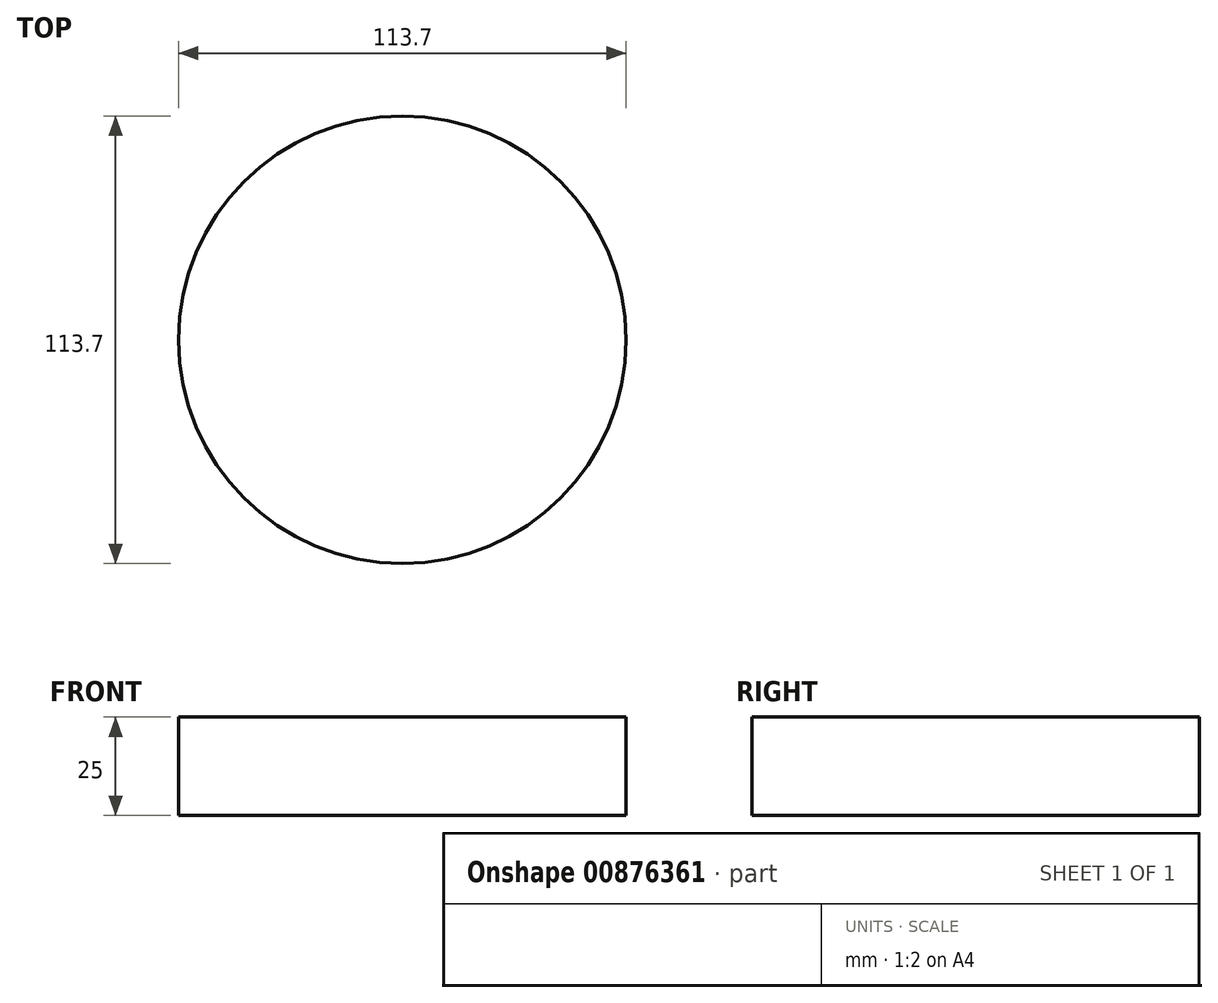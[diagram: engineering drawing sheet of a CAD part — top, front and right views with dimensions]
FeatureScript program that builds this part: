
annotation { "Feature Type Name" : "Feature", "Feature Type Description" : "" }
export const myFeature = defineFeature(function(context is Context, id is Id, definition is map)
    precondition{}
    {
        {
            var Q0;
            Q0=qCreatedBy(makeId("Top.planeOp"),FACE);
            var sketch = newSketch(context, id + "F0", { "sketchPlane" : qUnion([Q0])});
            skCircle(sketch, "E0", {"center": v(0, 0) * mm, "radius": 56.85 * mm});
            skLineSegment(sketch, "E1", {"start": v(0, 0) * mm, "end": v(-47.95, -30.54) * mm});
            skLineSegment(sketch, "E2", {"start": v(0, 0) * mm, "end": v(46.28, 29.47) * mm});
            skLineSegment(sketch, "E3", {"start": v(34.44, -45.23) * mm, "end": v(-46.7, -32.42) * mm});
            skLineSegment(sketch, "E4", {"start": v(-46.7, -32.42) * mm, "end": v(-47.95, -30.54) * mm});
            skLineSegment(sketch, "E5.left", {"start": v(46.28, 29.47) * mm, "end": v(46.28, 29.44) * mm});
            skLineSegment(sketch, "E6.trimOffspring", {"start": v(47.75, 29.44) * mm, "end": v(34.44, -45.23) * mm});
            skLineSegment(sketch, "E7", {"start": v(46.28, 29.47) * mm, "end": v(47.94, 30.55) * mm});
            skLineSegment(sketch, "E8", {"start": v(47.75, 29.44) * mm, "end": v(48.02, 30.42) * mm});
            skLineSegment(sketch, "E9", {"start": v(-40.73, -25.94) * mm, "end": v(-11.54, -25.94) * mm});
            skLineSegment(sketch, "E10", {"start": v(-11.54, -25.94) * mm, "end": v(-11.54, -7.35) * mm});
            skLineSegment(sketch, "E11", {"start": v(-11.54, -7.35) * mm, "end": v(16.49, -10.51) * mm});
            skLineSegment(sketch, "E12", {"start": v(16.49, -10.51) * mm, "end": v(19.04, 12.13) * mm});
            skLineSegment(sketch, "E13", {"start": v(19.04, 12.13) * mm, "end": v(37.83, 4.78) * mm});
            skLineSegment(sketch, "E14", {"start": v(37.83, 4.78) * mm, "end": v(43.12, 27.46) * mm});
            skLineSegment(sketch, "E15", {"start": v(-12.27, -37.85) * mm, "end": v(41.9, -3.34) * mm});
            skCircle(sketch, "E16", {"center": v(-39.45, 7.52) * mm, "radius": 14.41 * mm});
            skCircle(sketch, "E17", {"center": v(5.67, 37.76) * mm, "radius": 15.76 * mm});
            skLineSegment(sketch, "E18", {"start": v(-30.28, 18.64) * mm, "end": v(-5.76, 26.92) * mm});
            skLineSegment(sketch, "E19", {"start": v(-26.8, 14.44) * mm, "end": v(0, 23.06) * mm});
            skSolve(sketch);
        }
        {
            var Q0;
            Q0 = qSketchRegion(id + "F0", true);
            var Q1;
            {var subQ0=sQuery(id+"F0.wireOp",EDGE,"E16");var subQ1=makeQuery(id+"F0.imprint","INTERSECT",VERTEX,{"derivedFrom":[subQ0,sQuery(id+"F0.wireOp",EDGE,"E18")]});Q1=makeQuery(id+"F0.imprint","IMPRINT",FACE,{"disambiguationData":[TD([[makeQuery(id+"F0.imprint","IMPRINT",EDGE,{"disambiguationData":[TD([[subQ1,1.0]])],"derivedFrom":subQ0}),1.0]])]});}
            var Q2;
            {var subQ0=sQuery(id+"F0.wireOp",EDGE,"E17");var subQ1=makeQuery(id+"F0.imprint","INTERSECT",VERTEX,{"derivedFrom":[subQ0,sQuery(id+"F0.wireOp",EDGE,"E18")]});Q2=makeQuery(id+"F0.imprint","IMPRINT",FACE,{"disambiguationData":[TD([[makeQuery(id+"F0.imprint","IMPRINT",EDGE,{"disambiguationData":[TD([[subQ1,-1.0]])],"derivedFrom":subQ0}),1.0]])]});}
            var Q3;
            {var subQ0=sQuery(id+"F0.wireOp",EDGE,"E18");Q3=makeQuery(id+"F0.imprint","IMPRINT",FACE,{"disambiguationData":[TD([[makeQuery(id+"F0.imprint","IMPRINT",EDGE,{"derivedFrom":subQ0}),-1.0]])]});}
            var Q4;
            {var subQ0=sQuery(id+"F0.wireOp",EDGE,"E9");Q4=makeQuery(id+"F0.imprint","IMPRINT",FACE,{"disambiguationData":[TD([[makeQuery(id+"F0.imprint","IMPRINT",EDGE,{"derivedFrom":subQ0}),1.0]])]});}
            var Q5;
            {var subQ3=sQuery(id+"F0.wireOp",EDGE,"E11");Q5=makeQuery(id+"F0.imprint","IMPRINT",FACE,{"disambiguationData":[TD([[makeQuery(id+"F0.imprint","IMPRINT",EDGE,{"derivedFrom":subQ3}),1.0]])]});}
            var Q6;
            {var subQ0=sQuery(id+"F0.wireOp",EDGE,"E13");Q6=makeQuery(id+"F0.imprint","IMPRINT",FACE,{"disambiguationData":[TD([[makeQuery(id+"F0.imprint","IMPRINT",EDGE,{"derivedFrom":subQ0}),1.0]])]});}
            extrude(context, id + "F1", {"entities" : qUnion([Q0, Q1, Q2, Q3, Q4, Q5, Q6]), "depth" : 25 * mm, "offsetDistance" : 25 * mm});
        }
    });
